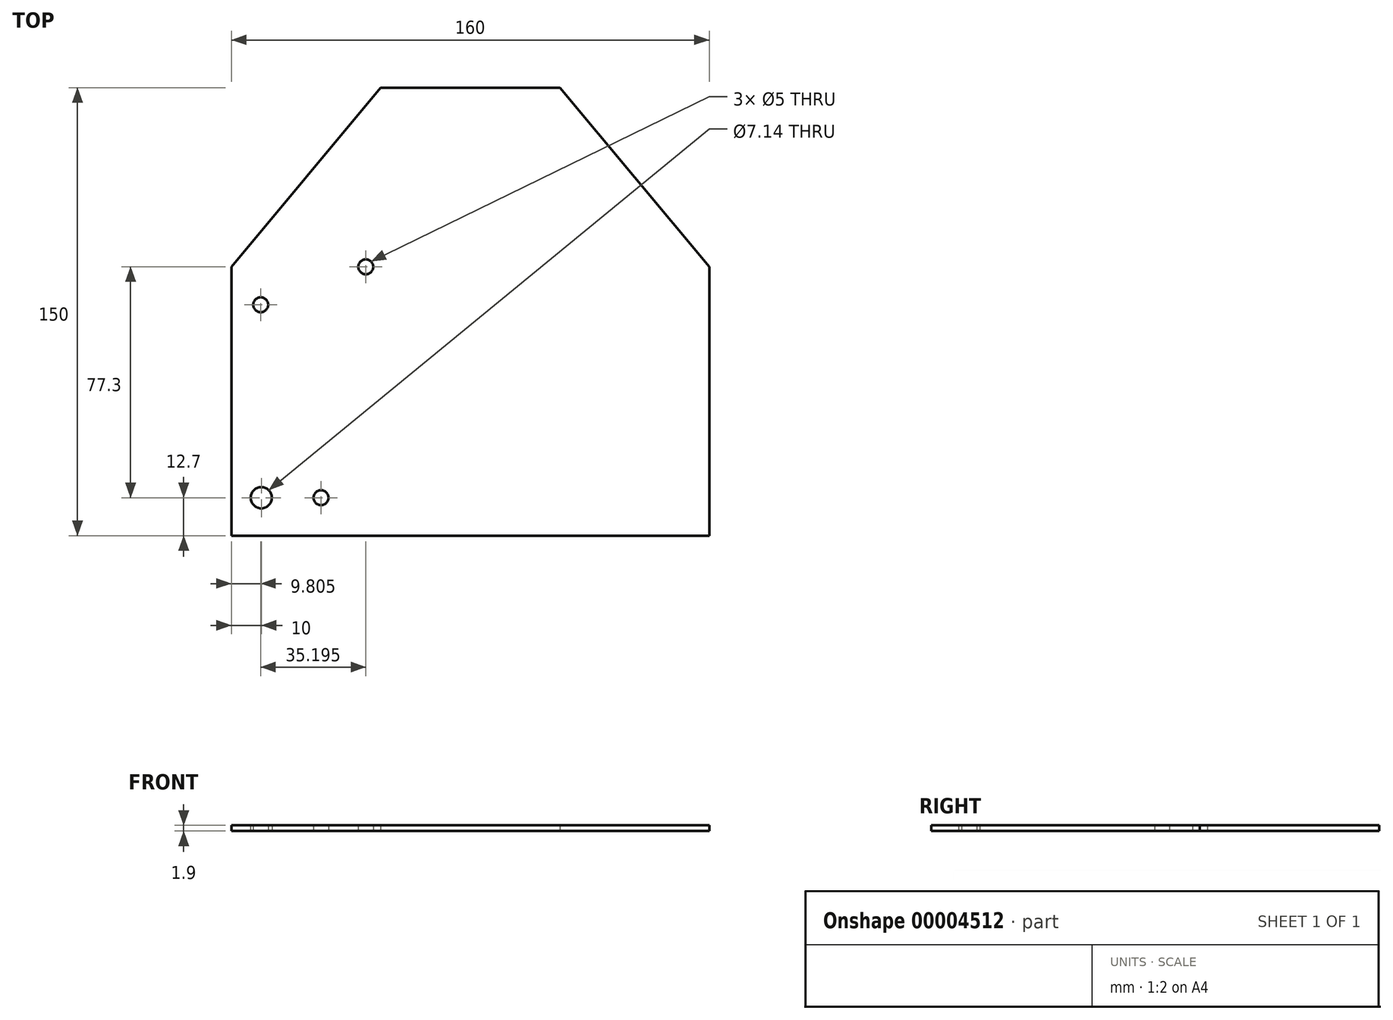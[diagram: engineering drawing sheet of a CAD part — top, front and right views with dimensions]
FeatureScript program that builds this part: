
annotation { "Feature Type Name" : "Feature", "Feature Type Description" : "" }
export const myFeature = defineFeature(function(context is Context, id is Id, definition is map)
    precondition{}
    {
        {
            var Q0;
            Q0=qCreatedBy(makeId("Top.planeOp"),FACE);
            var sketch = newSketch(context, id + "F0", { "sketchPlane" : qUnion([Q0])});
            skLineSegment(sketch, "E0", {"start": v(-80, -75) * mm, "end": v(80, -75) * mm});
            skLineSegment(sketch, "E1", {"start": v(80, -75) * mm, "end": v(80, 15) * mm});
            skLineSegment(sketch, "E2", {"start": v(80, 15) * mm, "end": v(30, 75) * mm});
            skLineSegment(sketch, "E3", {"start": v(-30, 75) * mm, "end": v(-80, 15) * mm});
            skLineSegment(sketch, "E4", {"start": v(-80, 15) * mm, "end": v(-80, -75) * mm});
            skLineSegment(sketch, "E5", {"start": v(-30, 75) * mm, "end": v(0, 75) * mm});
            skLineSegment(sketch, "E6", {"start": v(30, 75) * mm, "end": v(0, 75) * mm});
            skLineSegment(sketch, "E7", {"start": v(0, 75) * mm, "end": v(0, 0) * mm, "construction": true});
            skLineSegment(sketch, "E8", {"start": v(0, 0) * mm, "end": v(0, -75) * mm, "construction": true});
            skLineSegment(sketch, "E9", {"start": v(-80, 75) * mm, "end": v(-80, -75) * mm, "construction": true});
            skCircle(sketch, "E10", {"center": v(-70, -62.3) * mm, "radius": 3.57 * mm});
            skLineSegment(sketch, "E11", {"start": v(-70, -62.3) * mm, "end": v(-70, -75) * mm, "construction": true});
            skLineSegment(sketch, "E12", {"start": v(-70, -62.3) * mm, "end": v(-80, -62.3) * mm, "construction": true});
            skCircle(sketch, "E13", {"center": v(-70.2, 2.3) * mm, "radius": 2.5 * mm});
            skLineSegment(sketch, "E14", {"start": v(-70.2, 2.3) * mm, "end": v(-80, 2.3) * mm, "construction": true});
            skLineSegment(sketch, "E15", {"start": v(-70.2, 2.3) * mm, "end": v(-70, -75) * mm, "construction": true});
            skCircle(sketch, "E16", {"center": v(-50, -62.3) * mm, "radius": 2.5 * mm});
            skLineSegment(sketch, "E17", {"start": v(-50, -62.3) * mm, "end": v(-50, -75) * mm, "construction": true});
            skLineSegment(sketch, "E18", {"start": v(-50, -62.3) * mm, "end": v(-80, -62.3) * mm, "construction": true});
            skCircle(sketch, "E19", {"center": v(-35, 15) * mm, "radius": 2.5 * mm});
            skLineSegment(sketch, "E20", {"start": v(-35, 15) * mm, "end": v(-80, 15) * mm, "construction": true});
            skLineSegment(sketch, "E21", {"start": v(-35, 15) * mm, "end": v(-35, -75) * mm, "construction": true});
            skSolve(sketch);
        }
        {
            var Q0;
            Q0=makeQuery(id+"F0.imprint","IMPRINT",FACE,{"disambiguationData":[TD([[makeQuery(id+"F0.imprint","IMPRINT",EDGE,{"derivedFrom":sQuery(id+"F0.wireOp",EDGE,"E0")}),1.0]])]});
            extrude(context, id + "F1", {"entities" : qUnion([Q0]), "depth" : 1.9 * mm});
        }
    });
